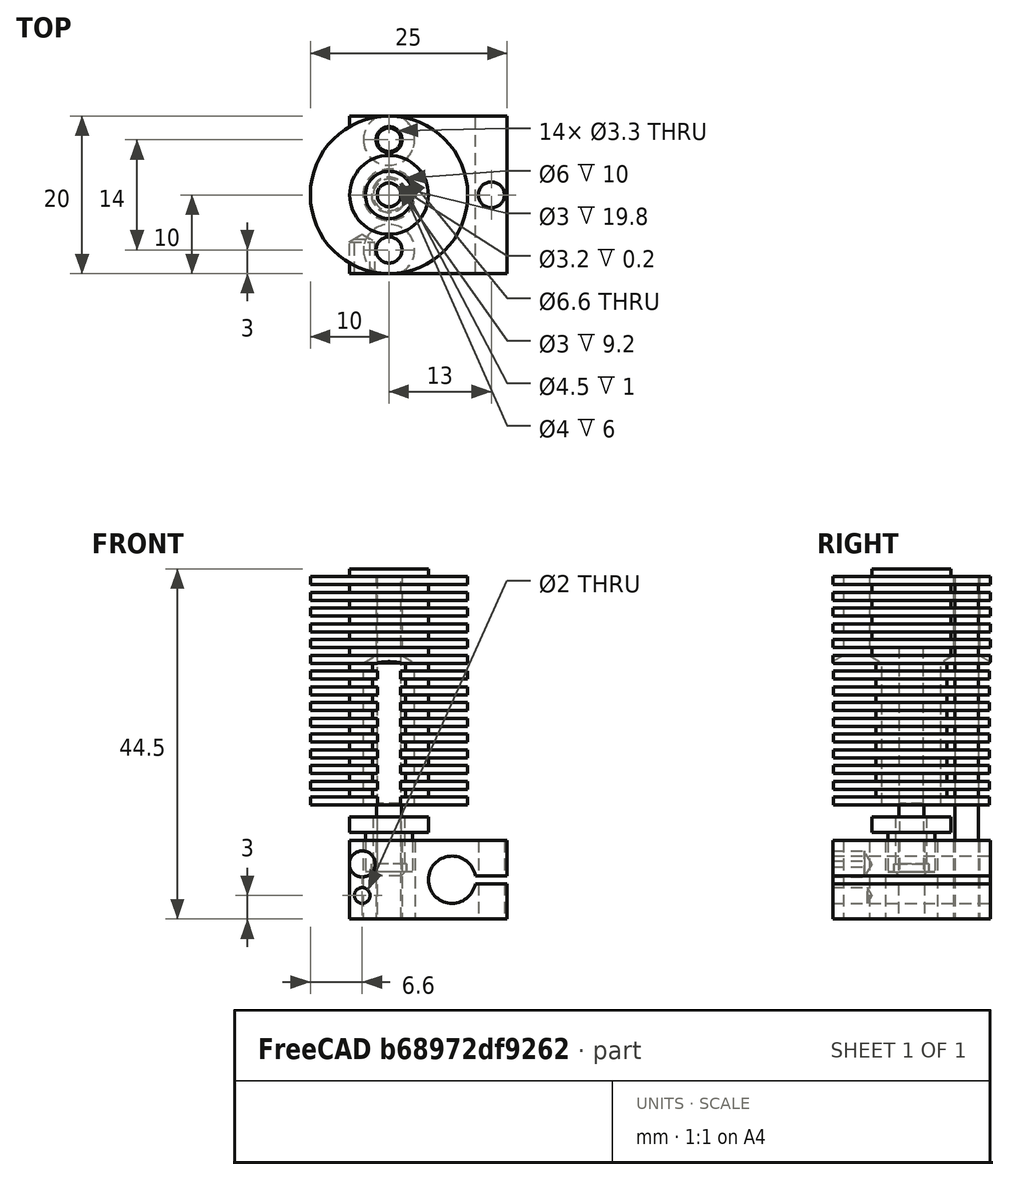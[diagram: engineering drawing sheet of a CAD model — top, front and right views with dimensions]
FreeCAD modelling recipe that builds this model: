
FCSTD DOCUMENT  (FreeCAD 0.18.4R)
Label: hotEndFinal
License: All rights reserved
LicenseURL: http://en.wikipedia.org/wiki/All_rights_reserved
objects: Sketcher::SketchObject×15, PartDesign::Hole×8, TechDraw::DrawViewDimension×7, PartDesign::Body×6, PartDesign::ShapeBinder×6, TechDraw::DrawViewPart×4, TechDraw::DrawViewSection×4, PartDesign::Revolution×3, PartDesign::Pad×2, TechDraw::DrawSVGTemplate×2, TechDraw::DrawProjGroupItem×2, TechDraw::DrawPage×2, PartDesign::Pocket×1, PartDesign::LinearPattern×1, PartDesign::Groove×1, PartDesign::FeatureBase×1, TechDraw::DrawProjGroup×1, TechDraw::DrawViewAnnotation×1
note: 59 computed .brp shape members not serialized (recipe doc carries the construction recipe); baked Part::Feature solids carry a one-line shape summary decoded from their .brp

FEATURE [Sketcher::SketchObject] Sketch
  MapMode = 5
  Support = -> [XY_Plane001]
  sketch-geometry (4):
    g0: LineSegment StartX=-5 StartY=-10 StartZ=0 EndX=15 EndY=-10 EndZ=0
    g1: LineSegment StartX=15 StartY=-10 StartZ=0 EndX=15 EndY=10 EndZ=0
    g2: LineSegment StartX=15 StartY=10 StartZ=0 EndX=-5 EndY=10 EndZ=0
    g3: LineSegment StartX=-5 StartY=10 StartZ=0 EndX=-5 EndY=-10 EndZ=0
  constraints (12):
    c: Coincident(g0,g1)
    c: Coincident(g1,g2)
    c: Coincident(g2,g3)
    c: Coincident(g3,g0)
    c: Horizontal(g0)
    c: Horizontal(g2)
    c: Vertical(g1)
    c: Vertical(g3)
    c: DistanceX(g2,g-1) = 5
    c: DistanceX(g2,g2) = 20
    c: DistanceY(g1,g1) = 20
    c: DistanceY(g-1,g2) = 10
FEATURE [PartDesign::Pad] Pad
  Length = 10
  Length2 = 100
  Profile = -> Sketch
  Type = 0
FEATURE [Sketcher::SketchObject] Sketch001
  MapMode = 5
  Placement = pos=(0,0,10) rot=(0,0,1;0rad)
  Support = -> [Pad]
  sketch-geometry (1):
    g0: Circle CenterX=0 CenterY=0 CenterZ=0 NormalX=0 NormalY=0 NormalZ=1 AngleXU=0 Radius=0.642747
  constraints (1):
    c: Coincident(g0,g-1)
FEATURE [PartDesign::Hole] Hole
  BaseFeature = -> Pad
  Depth = 25
  DepthType = 0
  Diameter = 6.6
  DrillPoint = 1
  DrillPointAngle = 118
  HoleCutCountersinkAngle = 90
  HoleCutDepth = 0
  HoleCutDiameter = 6
  HoleCutType = 0
  ModelActualThread = false
  Profile = -> Sketch001
  Tapered = false
  TaperedAngle = 90
  ThreadAngle = 0
  ThreadClass = 0
  ThreadCutOffInner = 0
  ThreadCutOffOuter = 0
  ThreadDirection = 0
  ThreadFit = 0
  ThreadPitch = 0
  ThreadSize = 7
  ThreadType = 1
  Threaded = false
FEATURE [Sketcher::SketchObject] Sketch002
  MapMode = 5
  Placement = pos=(0,0,10) rot=(0,0,1;0rad)
  Support = -> [Hole]
  sketch-geometry (4):
    g0: GeomPoint X=0 Y=7 Z=0
    g1: GeomPoint X=-1.8e-14 Y=-7 Z=0
    g2: Circle CenterX=0 CenterY=7 CenterZ=0 NormalX=0 NormalY=0 NormalZ=1 AngleXU=0 Radius=2.00415
    g3: Circle CenterX=-1.8e-14 CenterY=-7 CenterZ=0 NormalX=0 NormalY=0 NormalZ=1 AngleXU=0 Radius=1.74782
  constraints (5):
    c: PointOnObject(g0,g-2)
    c: DistanceY(g1,g0) = 14
    c: Symmetric(g0,g1,g-1)
    c: Coincident(g2,g0)
    c: Coincident(g3,g1)
FEATURE [PartDesign::Hole] Hole001
  BaseFeature = -> Hole
  Depth = 25
  DepthType = 1
  Diameter = 3.3
  DrillPoint = 1
  DrillPointAngle = 118
  HoleCutCountersinkAngle = 90
  HoleCutDepth = 0
  HoleCutDiameter = 3
  HoleCutType = 0
  ModelActualThread = false
  Profile = -> Sketch002
  Tapered = false
  TaperedAngle = 90
  ThreadAngle = 0
  ThreadClass = 0
  ThreadCutOffInner = 0
  ThreadCutOffOuter = 0
  ThreadDirection = 0
  ThreadFit = 0
  ThreadPitch = 0
  ThreadSize = 3
  ThreadType = 1
  Threaded = false
FEATURE [Sketcher::SketchObject] Sketch003
  MapMode = 5
  Placement = pos=(0,-10,0) rot=(1,0,0;1.5708rad)
  Support = -> [Hole001]
  sketch-geometry (1):
    g0: Circle CenterX=8 CenterY=5 CenterZ=0 NormalX=0 NormalY=0 NormalZ=1 AngleXU=0 Radius=2.00839
  constraints (2):
    c: DistanceY(g-1,g0) = 5
    c: DistanceX(g-1,g0) = 8
FEATURE [PartDesign::Hole] Hole002
  BaseFeature = -> Hole001
  Depth = 25
  DepthType = 1
  Diameter = 6
  DrillPoint = 1
  DrillPointAngle = 118
  HoleCutCountersinkAngle = 90
  HoleCutDepth = 0
  HoleCutDiameter = 0
  HoleCutType = 0
  ModelActualThread = false
  Profile = -> Sketch003
  Tapered = false
  TaperedAngle = 90
  ThreadAngle = 0
  ThreadClass = 0
  ThreadCutOffInner = 0
  ThreadCutOffOuter = 0
  ThreadDirection = 0
  ThreadFit = 0
  ThreadPitch = 0
  ThreadSize = 0
  ThreadType = 0
  Threaded = false
FEATURE [Sketcher::SketchObject] Sketch004
  ExternalGeometry = -> [Hole002]
  MapMode = 5
  Placement = pos=(15,0,0) rot=(0.57735,0.57735,0.57735;2.0944rad)
  Support = -> [Hole002]
  sketch-geometry (4):
    g0: LineSegment StartX=-10 StartY=5.5 StartZ=0 EndX=10 EndY=5.5 EndZ=0
    g1: LineSegment StartX=10 StartY=5.5 StartZ=0 EndX=10 EndY=4.5 EndZ=0
    g2: LineSegment StartX=10 StartY=4.5 StartZ=0 EndX=-10 EndY=4.5 EndZ=0
    g3: LineSegment StartX=-10 StartY=4.5 StartZ=0 EndX=-10 EndY=5.5 EndZ=0
  constraints (12):
    c: Coincident(g0,g1)
    c: Coincident(g1,g2)
    c: Coincident(g2,g3)
    c: Coincident(g3,g0)
    c: Horizontal(g0)
    c: Horizontal(g2)
    c: Vertical(g1)
    c: Vertical(g3)
    c: PointOnObject(g0,g-4)
    c: PointOnObject(g1,g-3)
    c: DistanceY(g1,g1) = 1
    c: DistanceY(g-1,g1) = 4.5
FEATURE [PartDesign::Pocket] Pocket
  BaseFeature = -> Hole002
  Length = 5
  Length2 = 100
  Profile = -> Sketch004
  Type = 2
FEATURE [Sketcher::SketchObject] Sketch005
  ExternalGeometry = -> [Pocket]
  MapMode = 5
  Placement = pos=(0,0,10) rot=(0,0,1;0rad)
  Support = -> [Pocket]
  sketch-geometry (1):
    g0: Circle CenterX=13 CenterY=0 CenterZ=0 NormalX=0 NormalY=0 NormalZ=1 AngleXU=0 Radius=1.08898
  constraints (2):
    c: PointOnObject(g0,g-1)
    c: DistanceX(g0,g-3) = 2
FEATURE [PartDesign::Hole] Hole003
  BaseFeature = -> Pocket
  Depth = 25
  DepthType = 0
  Diameter = 3.3
  DrillPoint = 1
  DrillPointAngle = 118
  HoleCutCountersinkAngle = 90
  HoleCutDepth = 0
  HoleCutDiameter = 3
  HoleCutType = 0
  ModelActualThread = false
  Profile = -> Sketch005
  Tapered = false
  TaperedAngle = 90
  ThreadAngle = 0
  ThreadClass = 0
  ThreadCutOffInner = 0
  ThreadCutOffOuter = 0
  ThreadDirection = 0
  ThreadFit = 0
  ThreadPitch = 0
  ThreadSize = 3
  ThreadType = 1
  Threaded = false
FEATURE [Sketcher::SketchObject] Sketch006
  ExternalGeometry = -> [Hole003]
  MapMode = 5
  Placement = pos=(0,-10,0) rot=(1,0,0;1.5708rad)
  Support = -> [Hole003]
  sketch-geometry (1):
    g0: Circle CenterX=-3.4 CenterY=7 CenterZ=0 NormalX=0 NormalY=0 NormalZ=1 AngleXU=0 Radius=1.5
  constraints (3):
    c: DistanceY(g0,g-3) = 3
    c: DistanceX(g-4,g0) = 1.6
    c: Diameter(g0) = 3
FEATURE [PartDesign::Hole] Hole004
  BaseFeature = -> Hole003
  Depth = 5
  DepthType = 0
  Diameter = 3.3
  DrillPoint = 1
  DrillPointAngle = 118
  HoleCutCountersinkAngle = 90
  HoleCutDepth = 0
  HoleCutDiameter = 3
  HoleCutType = 0
  ModelActualThread = false
  Profile = -> Sketch006
  Tapered = false
  TaperedAngle = 90
  ThreadAngle = 0
  ThreadClass = 0
  ThreadCutOffInner = 0
  ThreadCutOffOuter = 0
  ThreadDirection = 0
  ThreadFit = 0
  ThreadPitch = 0
  ThreadSize = 3
  ThreadType = 1
  Threaded = false
FEATURE [Sketcher::SketchObject] Sketch007
  ExternalGeometry = -> [Hole004]
  MapMode = 5
  Placement = pos=(0,-10,0) rot=(1,0,0;1.5708rad)
  Support = -> [Hole004]
  sketch-geometry (1):
    g0: Circle CenterX=-3.4 CenterY=3 CenterZ=0 NormalX=0 NormalY=0 NormalZ=1 AngleXU=0 Radius=0.765326
  constraints (2):
    c: DistanceX(g-3,g0) = 1.6
    c: DistanceY(g-1,g0) = 3
FEATURE [PartDesign::Hole] Hole005
  BaseFeature = -> Hole004
  Depth = 5
  DepthType = 0
  Diameter = 2
  DrillPoint = 1
  DrillPointAngle = 118
  HoleCutCountersinkAngle = 90
  HoleCutDepth = 0
  HoleCutDiameter = 0
  HoleCutType = 0
  ModelActualThread = false
  Profile = -> Sketch007
  Tapered = false
  TaperedAngle = 90
  ThreadAngle = 0
  ThreadClass = 0
  ThreadCutOffInner = 0
  ThreadCutOffOuter = 0
  ThreadDirection = 0
  ThreadFit = 0
  ThreadPitch = 0
  ThreadSize = 0
  ThreadType = 0
  Threaded = false
FEATURE [PartDesign::Body] Body  label="Heater Block"
  Group = -> [Sketch,Pad,Sketch001,Hole,Sketch002,Hole001,Sketch003,Hole002,Sketch004,Pocket,Sketch005,Hole003,Sketch006,Hole004,Sketch007,Hole005]
  Origin = -> Origin001
  Tip = -> Hole005
FEATURE [PartDesign::ShapeBinder] ShapeBinder
  Support = -> [Hole005]
  TraceSupport = false
FEATURE [Sketcher::SketchObject] Sketch011
  ExternalGeometry = -> [ShapeBinder]
  MapMode = 5
  Placement = pos=(0,6.8e-14,43.5) rot=(0,0,1;3.14159rad)
  sketch-geometry (2):
    g0: Circle CenterX=1.8e-14 CenterY=7 CenterZ=0 NormalX=0 NormalY=0 NormalZ=1 AngleXU=0 Radius=4.13634
    g1: Circle CenterX=0 CenterY=-7 CenterZ=0 NormalX=0 NormalY=0 NormalZ=1 AngleXU=0 Radius=3.845
  constraints (2):
    c: Coincident(g0,g-3)
    c: Coincident(g1,g-4)
FEATURE [PartDesign::ShapeBinder] ShapeBinder001
  Support = -> [Hole005]
  TraceSupport = false
FEATURE [Sketcher::SketchObject] Sketch012
  ExternalGeometry = -> [ShapeBinder001]
  MapMode = 5
  Placement = pos=(0,0,0) rot=(1,0,0;1.5708rad)
  Support = -> [XZ_Plane002]
  sketch-geometry (9):
    g0: LineSegment StartX=2 StartY=13 StartZ=0 EndX=5 EndY=13 EndZ=0
    g1: LineSegment StartX=5 StartY=13 StartZ=0 EndX=5 EndY=11 EndZ=0
    g2: LineSegment StartX=5 StartY=11 StartZ=0 EndX=3 EndY=11 EndZ=0
    g3: LineSegment StartX=3 StartY=11 StartZ=0 EndX=3 EndY=6 EndZ=0
    g4: LineSegment StartX=2 StartY=7 StartZ=0 EndX=2 EndY=13 EndZ=0
    g5: GeomPoint X=0 Y=12.9167 Z=0
    g6: LineSegment StartX=2 StartY=7 StartZ=0 EndX=2.25 EndY=7 EndZ=0
    g7: LineSegment StartX=2.25 StartY=7 StartZ=0 EndX=2.25 EndY=6 EndZ=0
    g8: LineSegment StartX=2.25 StartY=6 StartZ=0 EndX=3 EndY=6 EndZ=0
  constraints (26):
    c: Horizontal(g0)
    c: Coincident(g0,g1)
    c: Vertical(g1)
    c: Coincident(g1,g2)
    c: Horizontal(g2)
    c: Coincident(g2,g3)
    c: Vertical(g3)
    c: Coincident(g4,g0)
    c: Vertical(g4)
    c: PointOnObject(g5,g-2)
    c: DistanceX(g5,g0) = 2
    c: DistanceX(g5,g2) = 3
    c: DistanceX(g5,g0) = 5
    c: DistanceY(g1,g1) = 2
    c: DistanceY(g-4,g-4) = 0
    c: DistanceY(g-3,g2) = 1
    c: Coincident(g4,g6)
    c: Coincident(g6,g7)
    c: Vertical(g7)
    c: Coincident(g7,g8)
    c: Horizontal(g6)
    c: Horizontal(g8)
    c: Coincident(g3,g8)
    c: DistanceY(g3,g3) = 5
    c: DistanceX(g5,g6) = 2.25
    c: DistanceY(g7,g7) = 1
FEATURE [PartDesign::Revolution] Revolution001
  Angle = 360
  Axis = (0,2e-16,1)
  Base = (0,0,0)
  Placement = pos=(0,0,0) rot=(1,0,0;1.5708rad)
  Profile = -> Sketch012
  ReferenceAxis = -> Sketch012 [V_Axis]
  Reversed = true
FEATURE [PartDesign::Body] Body002  label="HeatbreakHolder"
  Group = -> [ShapeBinder001,Sketch012,Revolution001]
  Origin = -> Origin002
  Tip = -> Revolution001
FEATURE [PartDesign::ShapeBinder] ShapeBinder002
  Placement = pos=(0,0,0) rot=(1,0,0;1.5708rad)
  Support = -> [Revolution001]
  TraceSupport = false
FEATURE [Sketcher::SketchObject] Sketch013
  ExternalGeometry = -> [ShapeBinder002]
  MapMode = 5
  Placement = pos=(0,0,0) rot=(1,0,0;1.5708rad)
  Support = -> [XZ_Plane003]
  sketch-geometry (10):
    g0: LineSegment StartX=2 StartY=6 StartZ=0 EndX=2.2 EndY=6 EndZ=0
    g1: LineSegment StartX=2.2 StartY=6 StartZ=0 EndX=2.2 EndY=7 EndZ=0
    g2: LineSegment StartX=2.2 StartY=7 StartZ=0 EndX=2 EndY=7 EndZ=0
    g3: LineSegment StartX=2 StartY=7 StartZ=0 EndX=2 EndY=13 EndZ=0
    g4: LineSegment StartX=2 StartY=13 StartZ=0 EndX=1.6 EndY=13 EndZ=0
    g5: LineSegment StartX=1.6 StartY=13 StartZ=0 EndX=1.6 EndY=14.7 EndZ=0
    g6: LineSegment StartX=1.6 StartY=14.7 StartZ=0 EndX=1.5 EndY=14.7 EndZ=0
    g7: LineSegment StartX=1.5 StartY=14.7 StartZ=0 EndX=1.5 EndY=5.5 EndZ=0
    g8: LineSegment StartX=1.5 StartY=5.5 StartZ=0 EndX=2 EndY=6 EndZ=0
    g9: GeomPoint X=0 Y=6.62943 Z=0
  constraints (30):
    c: PointOnObject(g0,g-3)
    c: Coincident(g0,g1)
    c: PointOnObject(g1,g-4)
    c: Vertical(g1)
    c: Coincident(g1,g2)
    c: PointOnObject(g2,g-4)
    c: Coincident(g2,g3)
    c: Vertical(g3)
    c: Coincident(g3,g4)
    c: Horizontal(g4)
    c: Coincident(g4,g5)
    c: Coincident(g5,g6)
    c: Horizontal(g6)
    c: Coincident(g6,g7)
    c: Vertical(g7)
    c: Coincident(g7,g8)
    c: Coincident(g8,g0)
    c: Vertical(g5)
    c: Horizontal(g0)
    c: PointOnObject(g9,g-2)
    c: DistanceX(g9,g1) = 2.2
    c: DistanceX(g9,g2) = 2
    c: DistanceX(g9,g7) = 1.5
    c: Angle(g8,g7) = 0.785398
    c: DistanceX(g9,g0) = 2
    c: DistanceY(g7,g0) = 0.5
    c: DistanceY(g5,g5) = 1.7
    c: PointOnObject(g3,g-5)
    c: DistanceY(g0,g3) = 7
    c: DistanceX(g6,g6) = 0.1
FEATURE [PartDesign::Revolution] Revolution002
  Angle = 360
  Axis = (0,2e-16,1)
  Base = (0,0,0)
  Placement = pos=(0,0,0) rot=(1,0,0;1.5708rad)
  Profile = -> Sketch013
  ReferenceAxis = -> Sketch013 [V_Axis]
  Reversed = true
FEATURE [PartDesign::Body] Body003  label="Heatbreak"
  Group = -> [ShapeBinder002,Sketch013,Revolution002]
  Origin = -> Origin003
  Tip = -> Revolution002
FEATURE [PartDesign::ShapeBinder] ShapeBinder003
  Placement = pos=(0,0,0) rot=(1,0,0;1.5708rad)
  Support = -> [Revolution002]
  TraceSupport = false
FEATURE [Sketcher::SketchObject] Sketch008
  ExternalGeometry = -> [ShapeBinder003]
  MapMode = 5
  Placement = pos=(0,0,0) rot=(1,0,0;1.5708rad)
  Support = -> [XZ_Plane]
  sketch-geometry (7):
    g0: LineSegment StartX=0 StartY=14.5 StartZ=0 EndX=10 EndY=14.5 EndZ=0
    g1: LineSegment StartX=10 StartY=14.5 StartZ=0 EndX=10 EndY=15.5 EndZ=0
    g2: LineSegment StartX=10 StartY=15.5 StartZ=0 EndX=5 EndY=15.5 EndZ=0
    g3: LineSegment StartX=5 StartY=15.5 StartZ=0 EndX=5 EndY=16.5 EndZ=0
    g4: LineSegment StartX=5 StartY=16.5 StartZ=0 EndX=0 EndY=16.5 EndZ=0
    g5: LineSegment StartX=0 StartY=16.5 StartZ=0 EndX=0 EndY=14.5 EndZ=0
    g6: GeomPoint X=-0.454793 Y=14.7 Z=0
  constraints (19):
    c: PointOnObject(g0,g-2)
    c: Horizontal(g0)
    c: Coincident(g0,g1)
    c: Vertical(g1)
    c: Coincident(g1,g2)
    c: Horizontal(g2)
    c: Coincident(g2,g3)
    c: Vertical(g3)
    c: Coincident(g3,g4)
    c: Horizontal(g4)
    c: Coincident(g4,g5)
    c: Coincident(g5,g0)
    c: Vertical(g5)
    c: DistanceX(g4,g4) = 5
    c: DistanceX(g0,g0) = 10
    c: DistanceY(g3,g3) = 1
    c: DistanceY(g1,g1) = 1
    c: PointOnObject(g6,g-3)
    c: DistanceY(g0,g6) = 0.2
FEATURE [PartDesign::Revolution] Revolution  label="SingleFin"
  Angle = 360
  Axis = (0,2e-16,1)
  Base = (0,0,0)
  Placement = pos=(0,0,0) rot=(1,0,0;1.5708rad)
  Profile = -> Sketch008
  ReferenceAxis = -> Sketch008 [V_Axis]
  Reversed = true
FEATURE [PartDesign::LinearPattern] LinearPattern
  BaseFeature = -> Revolution
  Direction = -> Z_Axis
  Length = 28
  Occurrences = 15
  Originals = -> [Revolution]
  Placement = pos=(0,0,0) rot=(1,0,0;1.5708rad)
FEATURE [Sketcher::SketchObject] Sketch009
  ExternalGeometry = -> [LinearPattern]
  MapMode = 5
  Placement = pos=(0,0,0) rot=(1,0,0;1.5708rad)
  Support = -> [XZ_Plane]
  sketch-geometry (8):
    g0: LineSegment StartX=1.6 StartY=14.5 StartZ=0 EndX=1.6 EndY=14.7 EndZ=0
    g1: LineSegment StartX=1.6 StartY=14.7 StartZ=0 EndX=1.5 EndY=14.7 EndZ=0
    g2: LineSegment StartX=1.5 StartY=14.7 StartZ=0 EndX=1.5 EndY=34.5 EndZ=0
    g3: LineSegment StartX=1.5 StartY=34.5 StartZ=0 EndX=3 EndY=34.5 EndZ=0
    g4: LineSegment StartX=3 StartY=34.5 StartZ=0 EndX=3 EndY=44.5 EndZ=0
    g5: LineSegment StartX=3 StartY=44.5 StartZ=0 EndX=0 EndY=44.5 EndZ=0
    g6: LineSegment StartX=0 StartY=44.5 StartZ=0 EndX=0 EndY=14.5 EndZ=0
    g7: LineSegment StartX=0 StartY=14.5 StartZ=0 EndX=1.6 EndY=14.5 EndZ=0
  constraints (24):
    c: Coincident(g0,g1)
    c: Horizontal(g1)
    c: Coincident(g1,g2)
    c: Coincident(g2,g3)
    c: Horizontal(g3)
    c: Coincident(g3,g4)
    c: Vertical(g4)
    c: Coincident(g4,g5)
    c: PointOnObject(g5,g-2)
    c: Coincident(g5,g6)
    c: Vertical(g6)
    c: Coincident(g6,g7)
    c: Coincident(g7,g0)
    c: Horizontal(g5)
    c: Vertical(g0)
    c: Vertical(g2)
    c: DistanceX(g6,g1) = 1.5
    c: DistanceX(g7,g7) = 1.6
    c: DistanceX(g5,g5) = 3
    c: DistanceY(g6,g6) = 30
    c: DistanceY(g0,g0) = 0.2
    c: DistanceY(g4,g4) = 10
    c: PointOnObject(g0,g-3)
    c: Horizontal(g7)
FEATURE [PartDesign::Groove] Groove
  Angle = 360
  Axis = (0,2e-16,1)
  Base = (0,0,0)
  BaseFeature = -> LinearPattern
  Placement = pos=(0,0,0) rot=(1,0,0;1.5708rad)
  Profile = -> Sketch009
  ReferenceAxis = -> Sketch009 [V_Axis]
FEATURE [PartDesign::Hole] Hole007
  BaseFeature = -> Groove
  Depth = 25
  DepthType = 1
  Diameter = 3.3
  DrillPoint = 1
  DrillPointAngle = 118
  HoleCutCountersinkAngle = 90
  HoleCutDepth = 0
  HoleCutDiameter = 3
  HoleCutType = 0
  ModelActualThread = false
  Placement = pos=(0,0,0) rot=(1,0,0;1.5708rad)
  Profile = -> Sketch011
  Tapered = false
  TaperedAngle = 90
  ThreadAngle = 0
  ThreadClass = 0
  ThreadCutOffInner = 0
  ThreadCutOffOuter = 0
  ThreadDirection = 0
  ThreadFit = 0
  ThreadPitch = 0
  ThreadSize = 3
  ThreadType = 1
  Threaded = false
FEATURE [Sketcher::SketchObject] Sketch014
  ExternalGeometry = -> [Hole007]
  MapMode = 5
  Placement = pos=(0,2.3e-14,14.5) rot=(1,0,0;3.14159rad)
  Support = -> [Hole007]
  sketch-geometry (2):
    g0: Circle CenterX=-1.8e-14 CenterY=7 CenterZ=0 NormalX=0 NormalY=0 NormalZ=1 AngleXU=0 Radius=3.66013
    g1: Circle CenterX=0 CenterY=-7 CenterZ=0 NormalX=0 NormalY=0 NormalZ=1 AngleXU=0 Radius=3.65394
  constraints (2):
    c: Coincident(g-3,g1)
    c: Coincident(g0,g-4)
FEATURE [PartDesign::Hole] Hole008
  BaseFeature = -> Hole007
  Depth = 20
  DepthType = 0
  Diameter = 6.5
  DrillPoint = 1
  DrillPointAngle = 118
  HoleCutCountersinkAngle = 90
  HoleCutDepth = 0
  HoleCutDiameter = 0
  HoleCutType = 0
  ModelActualThread = false
  Placement = pos=(0,0,0) rot=(1,0,0;1.5708rad)
  Profile = -> Sketch014
  Tapered = false
  TaperedAngle = 90
  ThreadAngle = 0
  ThreadClass = 0
  ThreadCutOffInner = 0
  ThreadCutOffOuter = 0
  ThreadDirection = 0
  ThreadFit = 0
  ThreadPitch = 0
  ThreadSize = 0
  ThreadType = 0
  Threaded = false
FEATURE [PartDesign::Body] Body001  label="Heatsink"
  Group = -> [ShapeBinder003,Sketch008,Revolution,LinearPattern,Sketch009,Groove,ShapeBinder,Sketch011,Hole007,Sketch014,Hole008]
  Origin = -> Origin
  Tip = -> Hole008
FEATURE [PartDesign::ShapeBinder] ShapeBinder004
  Support = -> [Hole005]
  TraceSupport = false
FEATURE [Sketcher::SketchObject] Sketch015
  ExternalGeometry = -> [ShapeBinder004]
  MapMode = 5
  Placement = pos=(0,0,0) rot=(1,0,0;3.14159rad)
  Support = -> [ShapeBinder004]
  sketch-geometry (1):
    g0: Circle CenterX=0 CenterY=7 CenterZ=0 NormalX=0 NormalY=0 NormalZ=1 AngleXU=0 Radius=1.5
  constraints (2):
    c: Coincident(g0,g-3)
    c: Diameter(g0) = 3
FEATURE [PartDesign::ShapeBinder] ShapeBinder005
  Placement = pos=(0,0,0) rot=(1,0,0;1.5708rad)
  Support = -> [Hole008]
  TraceSupport = false
FEATURE [PartDesign::Pad] Pad001
  Length = 10
  Length2 = 100
  Profile = -> Sketch015
  Reversed = true
  Type = 3
  UpToFace = -> ShapeBinder005 [Face1]
FEATURE [PartDesign::Body] Body004  label="M3 Bolt 1"
  Group = -> [ShapeBinder004,ShapeBinder005,Sketch015,Pad001]
  Origin = -> Origin004
  Tip = -> Pad001
FEATURE [PartDesign::FeatureBase] Clone
  BaseFeature = -> Body004
  Placement = pos=(0,14,0) rot=(0,0,1;0rad)
FEATURE [PartDesign::Body] Body005  label="M3 Bolt 2"
  BaseFeature = -> Body004
  Group = -> [Clone]
  Origin = -> Origin005
  Tip = -> Clone
FEATURE [TechDraw::DrawSVGTemplate] Template
  EditableTexts = Designed_by_Name=Designed by Name; Drawing_number=Drawing number; FC-Date=Date; FC-SC=Scale; FC-SH=Sheet; FC-Title=Title; Subtitle=Subtitle; Weight=Weight
  Height = 210
  Orientation = 1
  Width = 297
FEATURE [TechDraw::DrawProjGroupItem] ProjItem  label="Front"
  CoarseView = false
  Direction = (0,-1,0)
  Focus = 100
  HardHidden = true
  IsoCount = 0
  IsoHidden = false
  IsoVisible = false
  LockPosition = true
  Perspective = false
  Rotation = 0
  RotationVector = (1,0,0)
  Scale = 2
  ScaleType = 2
  SeamHidden = false
  SeamVisible = false
  SmoothHidden = false
  SmoothVisible = false
  Source = -> [Body]
  Type = 0
  X = 0
  Y = 0
FEATURE [TechDraw::DrawProjGroupItem] ProjItem001  label="Top"
  CoarseView = false
  Direction = (0,0,1)
  Focus = 100
  HardHidden = true
  IsoCount = 0
  IsoHidden = true
  IsoVisible = false
  LockPosition = false
  Perspective = false
  Rotation = 0
  RotationVector = (1,0,0)
  Scale = 2
  ScaleType = 2
  SeamHidden = true
  SeamVisible = false
  SmoothHidden = true
  SmoothVisible = false
  Source = -> [Body]
  Type = 4
  X = 0
  Y = -55
FEATURE [TechDraw::DrawProjGroup] ProjGroup
  Anchor = -> ProjItem
  AutoDistribute = true
  LockPosition = false
  ProjectionType = 0
  Rotation = 0
  Scale = 2
  ScaleType = 0
  Source = -> [Body]
  Views = -> [ProjItem,ProjItem001]
  X = 91.232
  Y = 164.977
  spacingX = 15
  spacingY = 15
FEATURE [TechDraw::DrawViewDimension] Dimension
  Arbitrary = false
  FormatSpec = %.2f
  LockPosition = false
  MeasureType = 1
  OverTolerance = 0
  References2D = -> [ProjItem001]
  Rotation = 0
  Scale = 2
  ScaleType = 0
  Type = 1
  UnderTolerance = 0
  X = -32.4443
  Y = -29.728
FEATURE [TechDraw::DrawPage] Page
  KeepUpdated = true
  ProjectionType = 0
  Scale = 2
  Template = -> Template
  Views = -> [ProjGroup,Dimension]
FEATURE [TechDraw::DrawSVGTemplate] Template001
  EditableTexts = Designed_by_Name=Designed by Name; Drawing_number=Drawing number; FC-Date=Date; FC-SC=Scale; FC-SH=Sheet; FC-Title=Title; Subtitle=Subtitle; Weight=Weight
  Height = 210
  Orientation = 1
  Width = 297
FEATURE [TechDraw::DrawViewPart] View
  CoarseView = false
  Direction = (0,-1,0)
  Focus = 100
  HardHidden = true
  IsoCount = 0
  IsoHidden = false
  IsoVisible = false
  LockPosition = false
  Perspective = false
  Rotation = 0
  Scale = 2
  ScaleType = 0
  SeamHidden = false
  SeamVisible = false
  SmoothHidden = true
  SmoothVisible = false
  Source = -> [Body]
  X = 58.1512
  Y = 47.2093
FEATURE [TechDraw::DrawViewPart] View001
  CoarseView = false
  Direction = (0,-1,0)
  Focus = 100
  HardHidden = false
  IsoCount = 0
  IsoHidden = false
  IsoVisible = false
  LockPosition = false
  Perspective = false
  Rotation = 0
  Scale = 2
  ScaleType = 0
  SeamHidden = false
  SeamVisible = false
  SmoothHidden = false
  SmoothVisible = false
  Source = -> [Body002]
  X = 48.1124
  Y = 79.4961
FEATURE [TechDraw::DrawViewPart] View002
  CoarseView = false
  Direction = (0,-1,0)
  Focus = 100
  HardHidden = false
  IsoCount = 0
  IsoHidden = false
  IsoVisible = false
  LockPosition = false
  Perspective = false
  Rotation = 0
  Scale = 2
  ScaleType = 0
  SeamHidden = false
  SeamVisible = false
  SmoothHidden = false
  SmoothVisible = false
  Source = -> [Body003]
  X = 47.2984
  Y = 110.698
FEATURE [TechDraw::DrawViewPart] View003
  CoarseView = false
  Direction = (0,-1,0)
  Focus = 100
  HardHidden = false
  IsoCount = 0
  IsoHidden = false
  IsoVisible = false
  LockPosition = false
  Perspective = false
  Rotation = 0
  Scale = 2
  ScaleType = 0
  SeamHidden = false
  SeamVisible = false
  SmoothHidden = false
  SmoothVisible = false
  Source = -> [Body001]
  X = 47.5698
  Y = 162.519
FEATURE [TechDraw::DrawViewSection] Section  label="Section A - A"
  BaseView = -> View003
  CoarseView = false
  Direction = (1,0,0)
  Focus = 100
  FuseBeforeCut = true
  HardHidden = false
  HatchScale = 1
  IsoCount = 0
  IsoHidden = false
  IsoVisible = false
  LockPosition = false
  NameGeomPattern = Diamond
  Perspective = false
  Rotation = 0
  Scale = 2
  ScaleType = 0
  SeamHidden = false
  SeamVisible = false
  SectionDirection = 1
  SectionNormal = (1,0,0)
  SectionOrigin = (0,8.44e-14,29.5)
  SectionSymbol = A
  SmoothHidden = false
  SmoothVisible = false
  Source = -> [Body001]
  X = 118.655
  Y = 158.721
FEATURE [TechDraw::DrawViewSection] Section001  label="Section A - A001"
  BaseView = -> View002
  CoarseView = false
  Direction = (1,0,0)
  Focus = 100
  FuseBeforeCut = true
  HardHidden = false
  HatchScale = 1
  IsoCount = 0
  IsoHidden = false
  IsoVisible = false
  LockPosition = false
  NameGeomPattern = Diamond
  Perspective = false
  Rotation = 0
  Scale = 2
  ScaleType = 0
  SeamHidden = false
  SeamVisible = false
  SectionDirection = 1
  SectionNormal = (1,0,0)
  SectionOrigin = (0,4.4e-15,10.1)
  SectionSymbol = A
  SmoothHidden = false
  SmoothVisible = false
  Source = -> [Body003]
  X = 118.024
  Y = 102.495
FEATURE [TechDraw::DrawViewSection] Section002  label="Section A - A002"
  BaseView = -> View001
  CoarseView = false
  Direction = (1,0,0)
  Focus = 100
  FuseBeforeCut = true
  HardHidden = false
  HatchScale = 1
  IsoCount = 0
  IsoHidden = false
  IsoVisible = false
  LockPosition = false
  NameGeomPattern = Diamond
  Perspective = false
  Rotation = 0
  Scale = 2
  ScaleType = 0
  SeamHidden = false
  SeamVisible = false
  SectionDirection = 1
  SectionNormal = (1,0,0)
  SectionOrigin = (0,8e-15,9.5)
  SectionSymbol = A
  SmoothHidden = false
  SmoothVisible = false
  Source = -> [Body002]
  X = 118.655
  Y = 76.5116
FEATURE [TechDraw::DrawViewSection] Section003  label="Section A - A003"
  BaseView = -> View
  CoarseView = false
  Direction = (1,0,0)
  Focus = 100
  FuseBeforeCut = true
  HardHidden = false
  HatchScale = 1
  IsoCount = 0
  IsoHidden = false
  IsoVisible = false
  LockPosition = false
  NameGeomPattern = Diamond
  Perspective = false
  Rotation = 0
  Scale = 2
  ScaleType = 0
  SeamHidden = false
  SeamVisible = false
  SectionDirection = 1
  SectionNormal = (1,0,0)
  SectionOrigin = (0,0,5)
  SectionSymbol = A
  SmoothHidden = false
  SmoothVisible = false
  Source = -> [Body]
  X = 118.112
  Y = 47.4806
FEATURE [TechDraw::DrawViewDimension] Dimension001
  Arbitrary = false
  FormatSpec = %.2f
  LockPosition = false
  MeasureType = 1
  OverTolerance = 0
  References2D = -> [View001]
  Rotation = 0
  Scale = 2
  ScaleType = 0
  Type = 1
  UnderTolerance = 0
  X = 31.0885
  Y = -1.03352
FEATURE [TechDraw::DrawViewAnnotation] Annotation
  Font = osifont
  LineSpace = 80
  LockPosition = false
  MaxWidth = -1
  Rotation = 0
  Scale = 2
  ScaleType = 0
  Text = M
  TextSize = 4
  TextStyle = 0
  X = 69.0516
  Y = 79.0929
FEATURE [TechDraw::DrawViewDimension] Dimension002
  Arbitrary = false
  FormatSpec = %.2f
  LockPosition = false
  MeasureType = 1
  OverTolerance = 0
  References2D = -> [Section001]
  Rotation = 0
  Scale = 2
  ScaleType = 0
  Type = 1
  UnderTolerance = 0
  X = 37.4104
  Y = 17.0085
FEATURE [TechDraw::DrawViewDimension] Dimension003
  Arbitrary = false
  FormatSpec = %.2f
  LockPosition = false
  MeasureType = 1
  OverTolerance = 0
  References2D = -> [Section001]
  Rotation = 0
  Scale = 2
  ScaleType = 0
  Type = 1
  UnderTolerance = 0
  X = 36.2038
  Y = 3.47825
FEATURE [TechDraw::DrawViewDimension] Dimension004
  Arbitrary = false
  FormatSpec = %.2f
  LockPosition = false
  MeasureType = 1
  OverTolerance = 0
  References2D = -> [Section001]
  Rotation = 0
  Scale = 2
  ScaleType = 0
  Type = 1
  UnderTolerance = 0
  X = 37.4854
  Y = 10.4875
FEATURE [TechDraw::DrawViewDimension] Dimension005
  Arbitrary = false
  FormatSpec = %.2f
  LockPosition = false
  MeasureType = 1
  OverTolerance = 0
  References2D = -> [Section001]
  Rotation = 0
  Scale = 2
  ScaleType = 0
  Type = 2
  UnderTolerance = 0
  X = -26.6016
  Y = 9.50455
FEATURE [TechDraw::DrawViewDimension] Dimension006
  Arbitrary = false
  FormatSpec = %.2f
  LockPosition = false
  MeasureType = 1
  OverTolerance = 0
  References2D = -> [Section002]
  Rotation = 0
  Scale = 2
  ScaleType = 0
  Type = 1
  UnderTolerance = 0
  X = 34.5428
  Y = 8.70097
FEATURE [TechDraw::DrawPage] Page001  label="Overview"
  KeepUpdated = true
  ProjectionType = 0
  Scale = 2
  Template = -> Template001
  Views = -> [View,View001,View002,View003,Section,Section001,Section002,Section003,Dimension001,Annotation,Dimension002,Dimension003,Dimension004,Dimension005,Dimension006]
